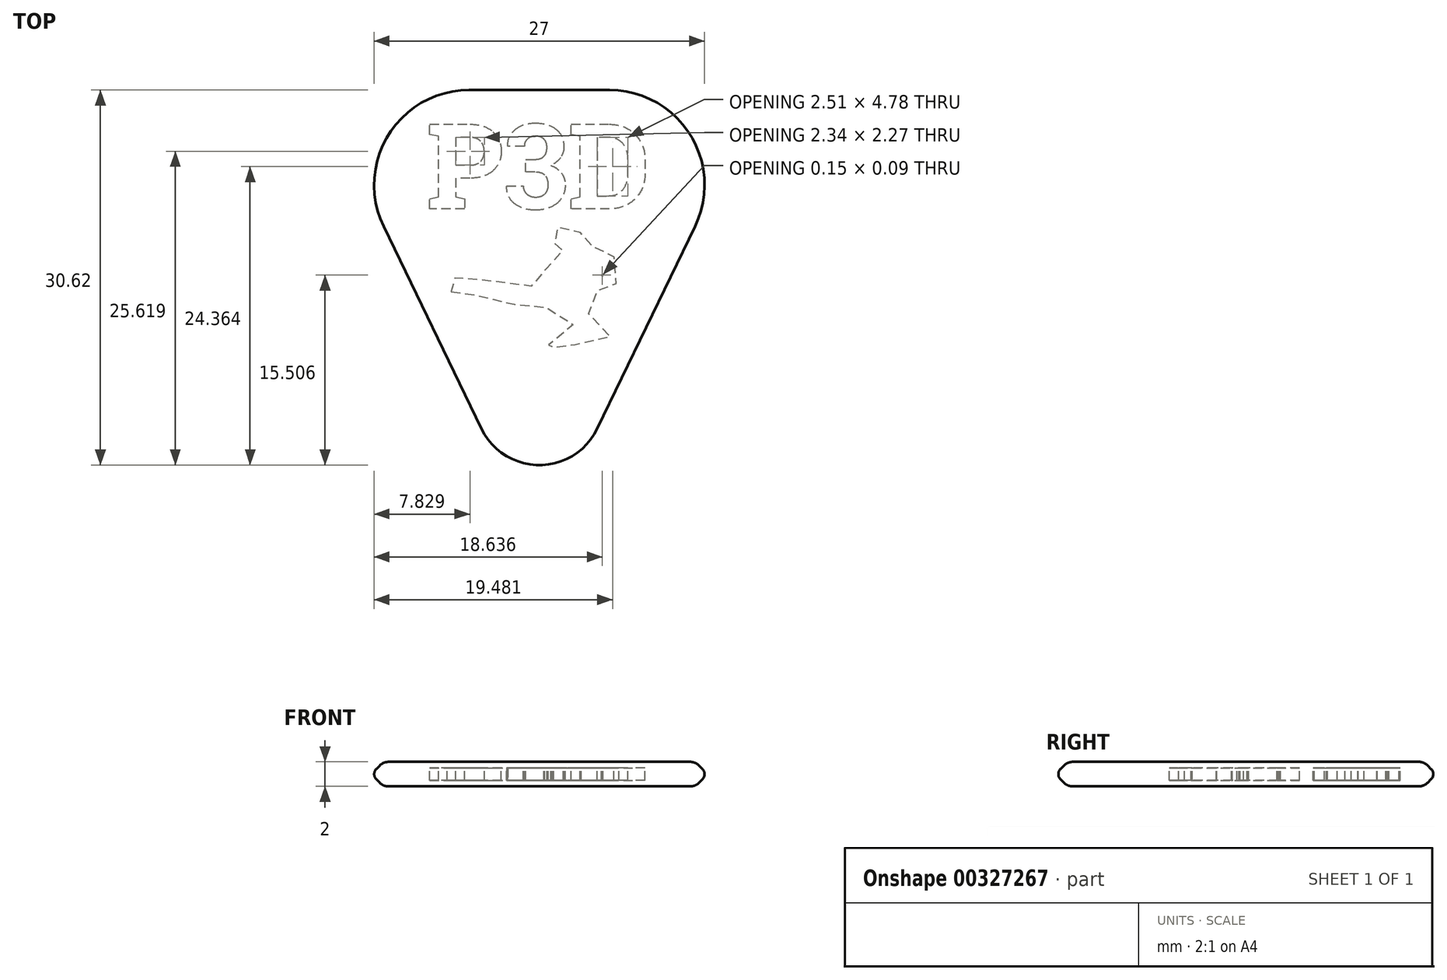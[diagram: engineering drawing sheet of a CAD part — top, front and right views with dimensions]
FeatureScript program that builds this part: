
annotation { "Feature Type Name" : "Feature", "Feature Type Description" : "" }
export const myFeature = defineFeature(function(context is Context, id is Id, definition is map)
    precondition{}
    {
        {
            var Q0;
            Q0=qCreatedBy(makeId("Top.planeOp"),FACE);
            var sketch = newSketch(context, id + "F0", { "sketchPlane" : qUnion([Q0])});
            skLineSegment(sketch, "E0", {"start": v(-5.74, 12.45) * mm, "end": v(5.74, 12.45) * mm});
            skLineSegment(sketch, "E1", {"start": v(12.95, 0.97) * mm, "end": v(4.95, -15.56) * mm});
            skLineSegment(sketch, "E2", {"start": v(-4.95, -15.56) * mm, "end": v(-12.95, 0.97) * mm});
            skPoint(sketch, "E3.visualSharp", {"position": v(-18.5, 12.45) * mm});
            skArc(sketch, "E3.filletArc", {"start": v(-5.74, 12.45) * mm, "mid": v(-12.52, 8.7) * mm, "end": v(-12.95, 0.97) * mm});
            skPoint(sketch, "E4.visualSharp", {"position": v(18.5, 12.45) * mm});
            skArc(sketch, "E4.filletArc", {"start": v(12.95, 0.97) * mm, "mid": v(12.52, 8.7) * mm, "end": v(5.74, 12.45) * mm});
            skPoint(sketch, "E5.visualSharp", {"position": v(0, -25.8) * mm});
            skArc(sketch, "E5.filletArc", {"start": v(-4.95, -15.56) * mm, "mid": v(0, -18.66) * mm, "end": v(4.95, -15.56) * mm});
            skSolve(sketch);
        }
        {
            var Q0;
            Q0=makeQuery(id+"F0.imprint","IMPRINT",FACE,{"disambiguationData":[TD([[makeQuery(id+"F0.imprint","IMPRINT",EDGE,{"derivedFrom":sQuery(id+"F0.wireOp",EDGE,"E0")}),-1.0]])]});
            extrude(context, id + "F1", {"entities" : qUnion([Q0]), "endBound" : BoundingType.SYMMETRIC, "depth" : 2 * mm});
        }
        {
            var Q0;
            Q0=makeQuery(id+"F1.opExtrude","CAP_EDGE",EDGE,{"disambiguationData":[OSD([sQuery(id+"F0.wireOp",EDGE,"E1")])],"isStart":false});
            var Q1;
            Q1=makeQuery(id+"F1.opExtrude","CAP_EDGE",EDGE,{"disambiguationData":[OSD([sQuery(id+"F0.wireOp",EDGE,"E1")])],"isStart":true});
            chamfer(context, id + "F2", {"entities" : qUnion([Q0, Q1]), "chamferType" : ChamferType.OFFSET_ANGLE, "width" : 1 * mm, "oppositeDirection" : false, "angle" : 45 * degree, "tangentPropagation" : true});
        }
        {
            var Q0;
            {var subQ0=sQuery(id+"F0.wireOp",EDGE,"E2");Q0=makeQuery(id+"F2.opChamfer","BLEND_EDGE",EDGE,{"blendedFrom":[makeQuery(id+"F1.opExtrude","CAP_EDGE",EDGE,{"disambiguationData":[OSD([subQ0])],"isStart":false}),makeQuery(id+"F1.opExtrude","CAP_FACE",FACE,{"disambiguationData":[OSD([sQuery(id+"F0.wireOp",EDGE,"E0"),sQuery(id+"F0.wireOp",EDGE,"E1"),subQ0,sQuery(id+"F0.wireOp",EDGE,"E3.filletArc"),sQuery(id+"F0.wireOp",EDGE,"E4.filletArc"),sQuery(id+"F0.wireOp",EDGE,"E5.filletArc")])],"isStart":false})],"blendedInto":[makeQuery(id+"F1.opExtrude","CAP_FACE",FACE,{"disambiguationData":[OSD([sQuery(id+"F0.wireOp",EDGE,"E0"),sQuery(id+"F0.wireOp",EDGE,"E1"),subQ0,sQuery(id+"F0.wireOp",EDGE,"E3.filletArc"),sQuery(id+"F0.wireOp",EDGE,"E4.filletArc"),sQuery(id+"F0.wireOp",EDGE,"E5.filletArc")])],"isStart":false})]});}
            var Q1;
            {var subQ0=sQuery(id+"F0.wireOp",EDGE,"E1");Q1=makeQuery(id+"F2.opChamfer","BLEND_EDGE",EDGE,{"blendedFrom":[makeQuery(id+"F1.opExtrude","CAP_EDGE",EDGE,{"disambiguationData":[OSD([subQ0])],"isStart":true}),makeQuery(id+"F1.opExtrude","CAP_FACE",FACE,{"disambiguationData":[OSD([sQuery(id+"F0.wireOp",EDGE,"E0"),subQ0,sQuery(id+"F0.wireOp",EDGE,"E2"),sQuery(id+"F0.wireOp",EDGE,"E3.filletArc"),sQuery(id+"F0.wireOp",EDGE,"E4.filletArc"),sQuery(id+"F0.wireOp",EDGE,"E5.filletArc")])],"isStart":true})],"blendedInto":[makeQuery(id+"F1.opExtrude","CAP_FACE",FACE,{"disambiguationData":[OSD([sQuery(id+"F0.wireOp",EDGE,"E0"),subQ0,sQuery(id+"F0.wireOp",EDGE,"E2"),sQuery(id+"F0.wireOp",EDGE,"E3.filletArc"),sQuery(id+"F0.wireOp",EDGE,"E4.filletArc"),sQuery(id+"F0.wireOp",EDGE,"E5.filletArc")])],"isStart":true})]});}
            fillet(context, id + "F3", {"entities" : qUnion([Q0, Q1]), "radius" : 1 * mm, "tangentPropagation" : true, "allowEdgeOverflow" : false});
        }
        {
            var Q0;
            Q0=qCreatedBy(makeId("Top.planeOp"),FACE);
            var sketch = newSketch(context, id + "F4", { "sketchPlane" : qUnion([Q0])});
            skText(sketch, "E6", { "text": "P3D", "fontName": "RobotoSlab-Bold.ttf"});
            const initialGuessF4  = {"E6": [-0.00923, 0.0025, 1, 0, 0.007]};
            skSetInitialGuess(sketch, initialGuessF4);
            skSolve(sketch);
        }
        {
            var Q0;
            Q0=qSketchRegion(id+"F4",true);
            extrude(context, id + "F5", {"entities" : qUnion([Q0]), "operationType" : NewBodyOperationType.REMOVE, "endBound" : BoundingType.SYMMETRIC, "oppositeDirection" : true, "depth" : 1 * mm, "offsetDistance" : 25 * mm});
        }
        {
            var Q0;
            {var subQ0=sQuery(id+"F0.wireOp",EDGE,"E2");Q0=makeQuery(id+"F2.opChamfer","BLEND_EDGE",EDGE,{"blendedFrom":[makeQuery(id+"F1.opExtrude","CAP_EDGE",EDGE,{"disambiguationData":[OSD([subQ0])],"isStart":true}),makeQuery(id+"F1.opExtrude","CAP_EDGE",EDGE,{"disambiguationData":[OSD([subQ0])],"isStart":false})],"blendedInto":[]});}
            fillet(context, id + "F6", {"entities" : qUnion([Q0]), "radius" : 0.6 * mm, "tangentPropagation" : true, "allowEdgeOverflow" : false});
        }
        {
            var Q0;
            Q0=qCreatedBy(makeId("Top.planeOp"),FACE);
            var sketch = newSketch(context, id + "F7", { "sketchPlane" : qUnion([Q0])});
            skFitSpline(sketch, "E7", {"points": [v(-7.2, -4.25) * mm, v(-6.7, -4.2) * mm, v(-5.3, -4.44) * mm, v(-5.04, -4.67) * mm, v(-2.61, -5.2) * mm, v(-0.33, -5.5) * mm, v(0.52, -5.53) * mm, v(1.43, -6.24) * mm, v(2.92, -7.01) * mm, v(3.38, -7.26) * mm, v(2.78, -7.56) * mm, v(1.13, -7.56) * mm, v(1.07, -8.14) * mm, v(0.58, -8.8) * mm, v(0.44, -9.24) * mm, v(0.63, -9.35) * mm, v(1.68, -8.36) * mm, v(2.75, -8.22) * mm, v(2.83, -8.53) * mm, v(4.62, -8.36) * mm, v(5.94, -7.78) * mm, v(5.92, -7.15) * mm, v(3.44, -5.58) * mm, v(4.32, -4.65) * mm, v(5.12, -3.74) * mm, v(5.52, -3.65) * mm, v(6.22, -3.61) * mm, v(6.48, -3.25) * mm, v(6.33, -2.01) * mm, v(5.71, -0.78) * mm, v(4.94, -0.46) * mm, v(3.95, -0.56) * mm, v(3.57, -0.3) * mm, v(3.42, 0.25) * mm, v(3.05, 1.1) * mm, v(2.03, 1.23) * mm, v(1.21, 0.7) * mm, v(1.15, 0.13) * mm, v(1.12, -0.38) * mm, v(1.41, -0.28) * mm, v(1.46, -0.46) * mm, v(1.7, -0.46) * mm, v(1.79, -0.83) * mm, v(1.93, -0.9) * mm, v(1.93, -1.1) * mm, v(1.3, -1.47) * mm, v(0.4, -2.88) * mm, v(0.36, -3.42) * mm, v(-1.2, -3.82) * mm, v(-4.92, -3.29) * mm, v(-5.24, -3.5) * mm, v(-6.6, -3.37) * mm, v(-7.21, -3) * mm, v(-7.54, -3.54) * mm, v(-7.2, -4.25) * mm]});
            skFitSpline(sketch, "E8", {"points": [v(5.15, -2.86) * mm, v(5.06, -2.93) * mm, v(5.11, -2.95) * mm, v(5.21, -2.93) * mm, v(5.15, -2.86) * mm]});
            skSolve(sketch);
        }
        {
            var Q0;
            Q0=qSketchRegion(id+"F7",true);
            var Q1;
            Q1=makeQuery(id+"F7.imprint","IMPRINT",FACE,{"disambiguationData":[TD([[makeQuery(id+"F7.imprint","IMPRINT",EDGE,{"derivedFrom":sQuery(id+"F7.wireOp",EDGE,"b4bf5cf7-47f6-4e07-859f-e1e6065c9dbf.0")}),-1.0]])]});
            var Q2;
            Q2=makeQuery(id+"F7.imprint","IMPRINT",FACE,{"disambiguationData":[TD([[makeQuery(id+"F7.imprint","IMPRINT",EDGE,{"derivedFrom":sQuery(id+"F7.wireOp",EDGE,"6f85d2ec-8929-457e-84c4-58013a10ac05.0")}),-1.0]])]});
            extrude(context, id + "F8", {"entities" : qUnion([Q0, Q1, Q2]), "operationType" : NewBodyOperationType.REMOVE, "endBound" : BoundingType.SYMMETRIC, "oppositeDirection" : true, "depth" : 1 * mm, "offsetDistance" : 25 * mm});
        }
    });
